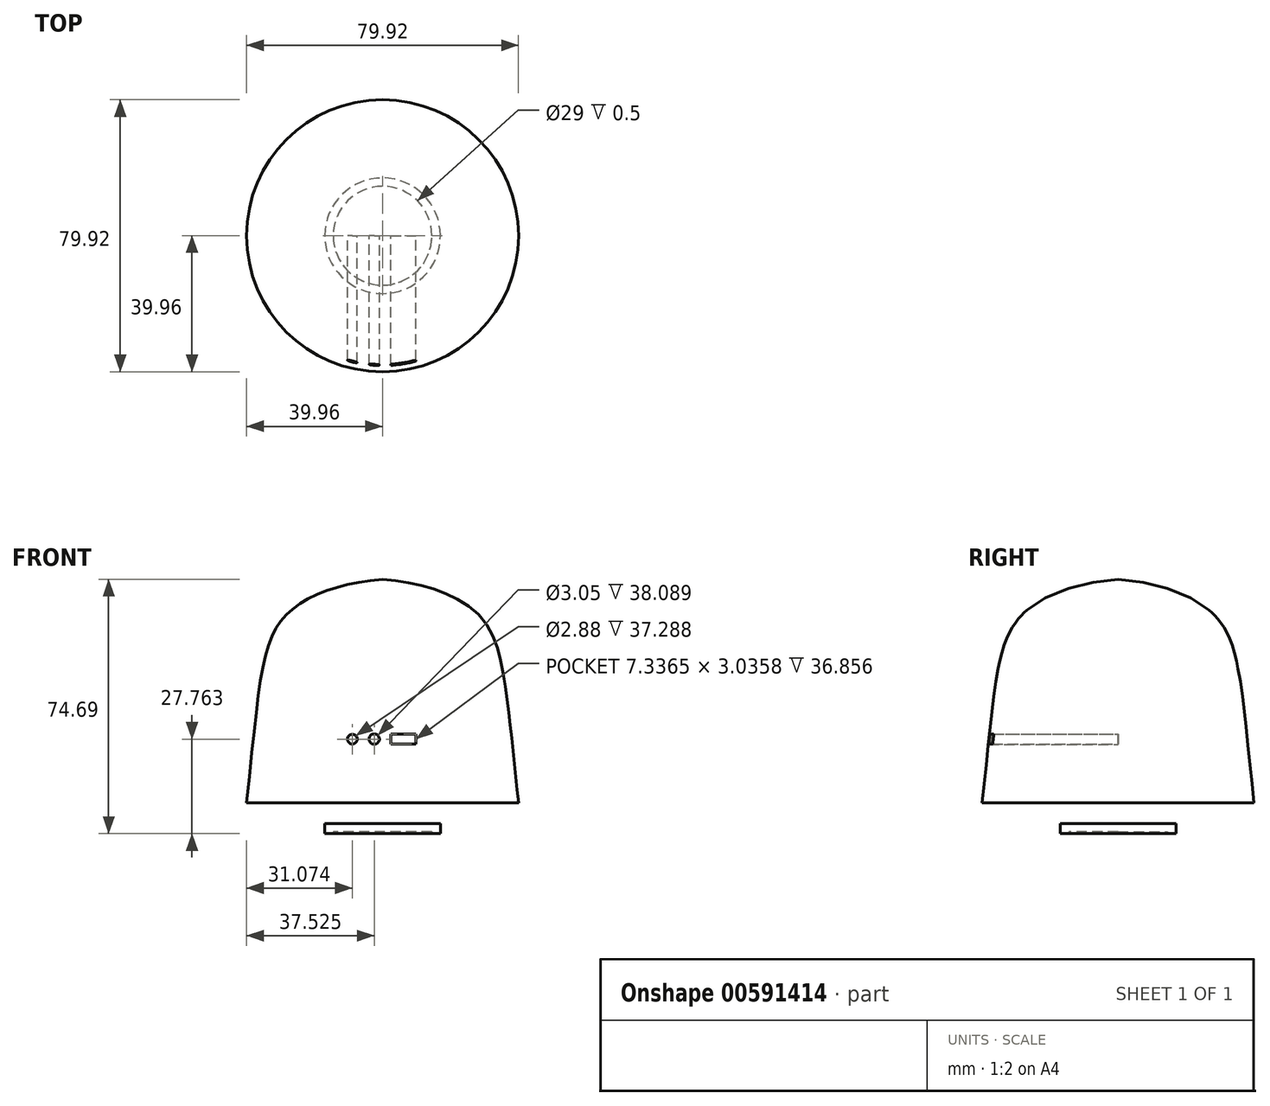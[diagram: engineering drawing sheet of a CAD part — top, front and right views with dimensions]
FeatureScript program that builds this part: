
annotation { "Feature Type Name" : "Feature", "Feature Type Description" : "" }
export const myFeature = defineFeature(function(context is Context, id is Id, definition is map)
    precondition{}
    {
        {
            var Q0;
            Q0=qCreatedBy(makeId("Front.planeOp"),FACE);
            var sketch = newSketch(context, id + "F0", { "sketchPlane" : qUnion([Q0])});
            skLineSegment(sketch, "E0", {"start": v(0, 0) * mm, "end": v(0, 65) * mm, "construction": true});
            skLineSegment(sketch, "E1", {"start": v(0, 65) * mm, "end": v(-27.5, 65) * mm, "construction": true});
            skLineSegment(sketch, "E2", {"start": v(-27.5, 65) * mm, "end": v(-27.5, 0) * mm, "construction": true});
            skLineSegment(sketch, "E3", {"start": v(-27.5, 0) * mm, "end": v(0, 0) * mm, "construction": true});
            skLineSegment(sketch, "E4", {"start": v(-27.5, 9) * mm, "end": v(0, 9) * mm, "construction": true});
            skFitSpline(sketch, "E5", {"points": [v(0, 74.7) * mm, v(-27.5, 65) * mm, v(-39.96, 9) * mm], "startDerivative": vector(-83.23, -6.08) * mm, "endDerivative": vector(-20.24, -187.2) * mm});
            skLineSegment(sketch, "E6", {"start": v(-39.96, 9) * mm, "end": v(0, 9) * mm});
            skLineSegment(sketch, "E7.bottom", {"start": v(-6, 9) * mm, "end": v(0, 9) * mm});
            skLineSegment(sketch, "E7.top", {"start": v(-6, 3) * mm, "end": v(0, 3) * mm});
            skLineSegment(sketch, "E7.left", {"start": v(-6, 9) * mm, "end": v(-6, 3) * mm});
            skLineSegment(sketch, "E7.right", {"start": v(0, 9) * mm, "end": v(0, 3) * mm});
            skLineSegment(sketch, "E8.bottom", {"start": v(0, 3) * mm, "end": v(-17, 3) * mm});
            skLineSegment(sketch, "E8.top", {"start": v(0, 0) * mm, "end": v(-17, 0) * mm});
            skLineSegment(sketch, "E8.left", {"start": v(0, 3) * mm, "end": v(0, 0) * mm});
            skLineSegment(sketch, "E8.right", {"start": v(-17, 3) * mm, "end": v(-17, 0) * mm});
            skLineSegment(sketch, "E9", {"start": v(0, 9) * mm, "end": v(0, 74.7) * mm});
            skSolve(sketch);
        }
        {
            var Q0;
            Q0=makeQuery(id+"F0.imprint","IMPRINT",FACE,{"disambiguationData":[TD([[makeQuery(id+"F0.imprint","IMPRINT",EDGE,{"derivedFrom":sQuery(id+"F0.wireOp",EDGE,"E7.bottom")}),-1.0]])]});
            var Q1;
            Q1=makeQuery(id+"F0.imprint","IMPRINT",FACE,{"disambiguationData":[TD([[makeQuery(id+"F0.imprint","IMPRINT",EDGE,{"derivedFrom":sQuery(id+"F0.wireOp",EDGE,"E8.top")}),-1.0]])]});
            var Q2;
            Q2=makeQuery(id+"F0.imprint","IMPRINT",FACE,{"disambiguationData":[TD([[makeQuery(id+"F0.imprint","IMPRINT",EDGE,{"derivedFrom":sQuery(id+"F0.wireOp",EDGE,"E5")}),1.0]])]});
            var Q3;
            Q3=sQuery(id+"F0.wireOp",EDGE,"E0");
            revolve(context, id + "F1", {"entities" : qUnion([Q0, Q1, Q2]), "axis" : qUnion([Q3]), "revolveType" : RevolveType.FULL});
        }
        {
            var Q0;
            Q0=qCreatedBy(makeId("Front.planeOp"),FACE);
            var sketch = newSketch(context, id + "F2", { "sketchPlane" : qUnion([Q0])});
            skCircle(sketch, "E10", {"center": v(-8.89, 27.76) * mm, "radius": 1.44 * mm});
            skCircle(sketch, "E11", {"center": v(-2.43, 27.76) * mm, "radius": 1.52 * mm});
            skLineSegment(sketch, "E12.bottom", {"start": v(2.5, 29.28) * mm, "end": v(9.83, 29.28) * mm});
            skLineSegment(sketch, "E12.top", {"start": v(2.5, 26.25) * mm, "end": v(9.83, 26.25) * mm});
            skLineSegment(sketch, "E12.left", {"start": v(2.5, 29.28) * mm, "end": v(2.5, 26.25) * mm});
            skLineSegment(sketch, "E12.right", {"start": v(9.83, 29.28) * mm, "end": v(9.83, 26.25) * mm});
            skSolve(sketch);
        }
        {
            var Q0;
            Q0=makeQuery(id+"F1.opRevolve","SWEPT_FACE",FACE,{"disambiguationData":[OSD([sQuery(id+"F0.wireOp",EDGE,"E8.top")])]});
            shell(context, id + "F3", {"entities" : qUnion([Q0]), "thickness" : 2.5 * mm});
        }
        {
            var Q0;
            Q0 = qSketchRegion(id + "F2", true);
            extrude(context, id + "F4", {"entities" : qUnion([Q0]), "operationType" : NewBodyOperationType.REMOVE, "depth" : 39 * mm, "offsetDistance" : 25 * mm});
        }
    });
